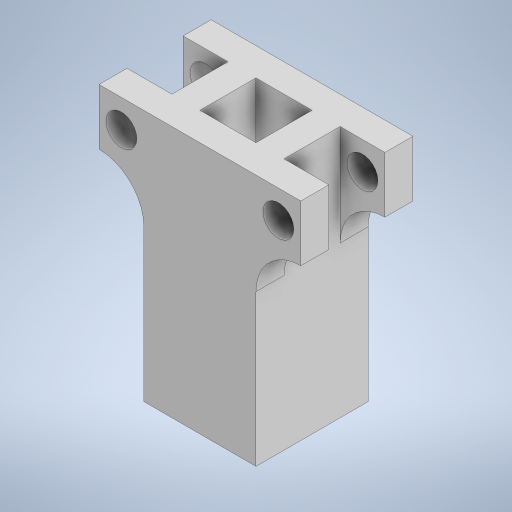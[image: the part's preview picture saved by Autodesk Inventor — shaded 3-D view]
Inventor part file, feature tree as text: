
AUTODESK INVENTOR PART (.ipt)
format: ipt  version: 2023 (Build 270158000, 158)  size: 278,016 bytes
history: native  units: mm
features: extrude x3, sketch x2, fillet x1
ambient origin geometry x8: Origin, YZ Plane, XZ Plane, XY Plane, X Axis, Y Axis, Z Axis, Center Point
bodies: Solido1 (feature_tree)
feature tree (6):
  sketch  "Schizzo1"
  extrude  "Estrusione1"  Depth=20.0mm
  extrude  "Estrusione2"  Depth=10.0mm
  fillet  "Raccordo1"  Radius=8.0mm
  extrude  "Estrusione3"  Depth=5.0mm
  sketch  "Schizzo2"
